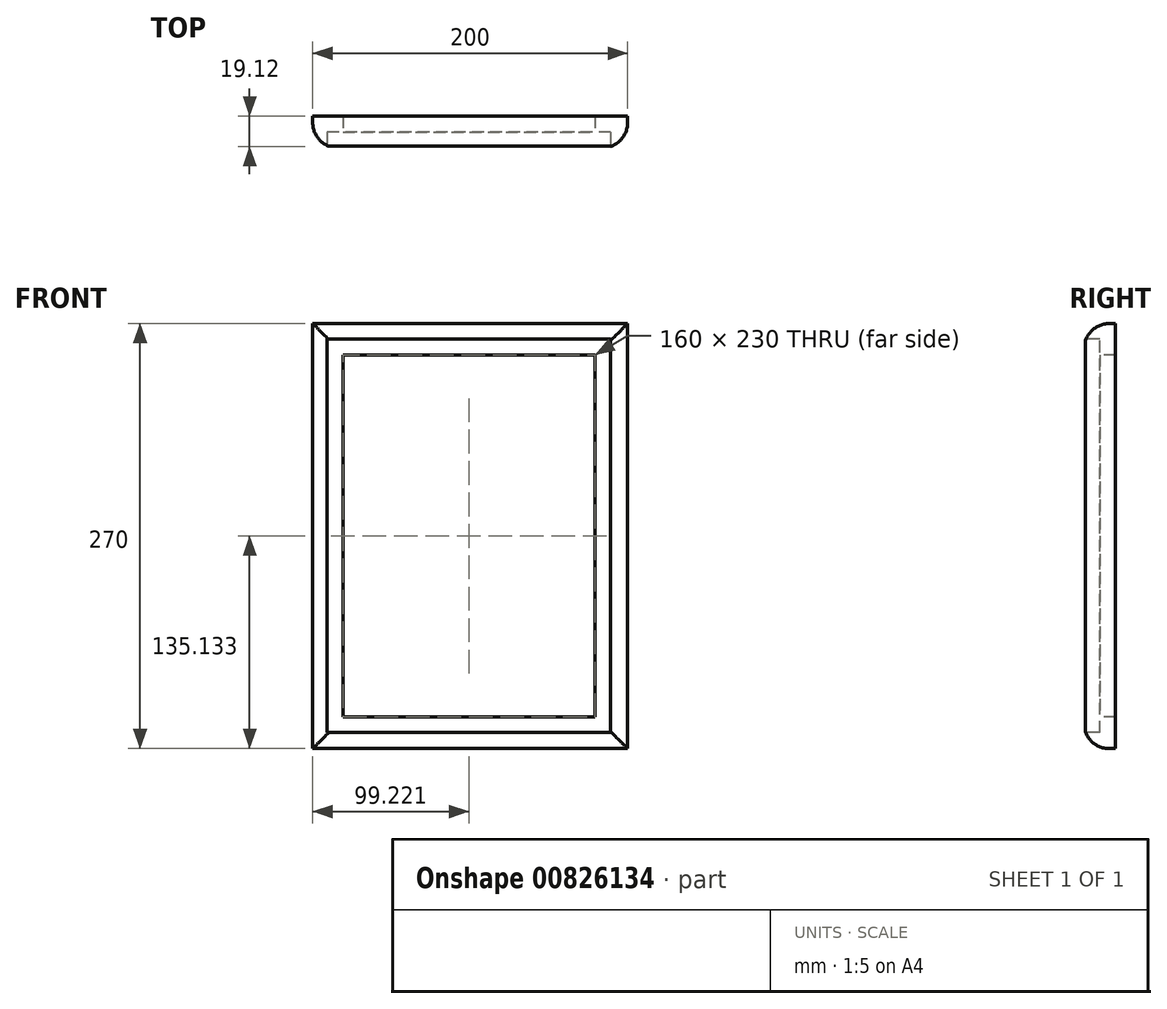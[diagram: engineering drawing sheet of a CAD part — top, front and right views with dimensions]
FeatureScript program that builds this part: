
annotation { "Feature Type Name" : "Feature", "Feature Type Description" : "" }
export const myFeature = defineFeature(function(context is Context, id is Id, definition is map)
    precondition{}
    {
        {
            var Q0;
            Q0=qCreatedBy(makeId("Front.planeOp"),FACE);
            var sketch = newSketch(context, id + "F0", { "sketchPlane" : qUnion([Q0])});
            skLineSegment(sketch, "E0.bottom", {"start": v(78.23, -133.71) * mm, "end": v(-121.77, -133.71) * mm});
            skLineSegment(sketch, "E0.top", {"start": v(78.23, 136.29) * mm, "end": v(-121.77, 136.29) * mm});
            skLineSegment(sketch, "E0.left", {"start": v(78.23, -133.71) * mm, "end": v(78.23, 136.29) * mm});
            skLineSegment(sketch, "E0.right", {"start": v(-121.77, -133.71) * mm, "end": v(-121.77, 136.29) * mm});
            skSolve(sketch);
        }
        {
            var Q0;
            Q0 = qSketchRegion(id + "F0", true);
            extrude(context, id + "F1", {"entities" : qUnion([Q0]), "depth" : 20 * mm, "offsetDistance" : 25 * mm});
        }
        {
            var Q0;
            Q0=makeQuery(id+"F1.opExtrude","CAP_FACE",FACE,{"disambiguationData":[OSD([sQuery(id+"F0.wireOp",EDGE,"E0.bottom"),sQuery(id+"F0.wireOp",EDGE,"E0.top"),sQuery(id+"F0.wireOp",EDGE,"E0.left"),sQuery(id+"F0.wireOp",EDGE,"E0.right")])],"isStart":false});
            var sketch = newSketch(context, id + "F2", { "sketchPlane" : qUnion([Q0])});
            skLineSegment(sketch, "E1.bottom", {"start": v(67.45, -123.58) * mm, "end": v(-112.55, -123.58) * mm});
            skLineSegment(sketch, "E1.top", {"start": v(67.45, 126.42) * mm, "end": v(-112.55, 126.42) * mm});
            skLineSegment(sketch, "E1.left", {"start": v(67.45, -123.58) * mm, "end": v(67.45, 126.42) * mm});
            skLineSegment(sketch, "E1.right", {"start": v(-112.55, -123.58) * mm, "end": v(-112.55, 126.42) * mm});
            skSolve(sketch);
        }
        {
            var Q0;
            Q0 = qSketchRegion(id + "F2", true);
            extrude(context, id + "F3", {"entities" : qUnion([Q0]), "operationType" : NewBodyOperationType.REMOVE, "oppositeDirection" : true, "depth" : 10 * mm, "offsetDistance" : 25 * mm});
        }
        {
            var Q0;
            Q0=makeQuery(id+"F3.boolean.opBoolean","COPY",FACE,{"derivedFrom":makeQuery(id+"F3.opExtrude","CAP_FACE",FACE,{"disambiguationData":[OSD([sQuery(id+"F2.wireOp",EDGE,"E1.bottom"),sQuery(id+"F2.wireOp",EDGE,"E1.top"),sQuery(id+"F2.wireOp",EDGE,"E1.left"),sQuery(id+"F2.wireOp",EDGE,"E1.right")])],"isStart":false})});
            var sketch = newSketch(context, id + "F4", { "sketchPlane" : qUnion([Q0])});
            skLineSegment(sketch, "E2.bottom", {"start": v(-102.55, 116.42) * mm, "end": v(57.45, 116.42) * mm});
            skLineSegment(sketch, "E2.top", {"start": v(-102.55, -113.58) * mm, "end": v(57.45, -113.58) * mm});
            skLineSegment(sketch, "E2.left", {"start": v(-102.55, 116.42) * mm, "end": v(-102.55, -113.58) * mm});
            skLineSegment(sketch, "E2.right", {"start": v(57.45, 116.42) * mm, "end": v(57.45, -113.58) * mm});
            skSolve(sketch);
        }
        {
            var Q0;
            Q0 = qSketchRegion(id + "F4", true);
            extrude(context, id + "F5", {"entities" : qUnion([Q0]), "operationType" : NewBodyOperationType.REMOVE, "oppositeDirection" : true, "depth" : 25 * mm, "offsetDistance" : 25 * mm});
        }
        {
            var Q0;
            Q0=makeQuery(id+"F1.opExtrude","CAP_EDGE",EDGE,{"disambiguationData":[OSD([sQuery(id+"F0.wireOp",EDGE,"E0.right")])],"isStart":false});
            var Q1;
            Q1=makeQuery(id+"F1.opExtrude","CAP_EDGE",EDGE,{"disambiguationData":[OSD([sQuery(id+"F0.wireOp",EDGE,"E0.top")])],"isStart":false});
            var Q2;
            Q2=makeQuery(id+"F1.opExtrude","CAP_EDGE",EDGE,{"disambiguationData":[OSD([sQuery(id+"F0.wireOp",EDGE,"E0.left")])],"isStart":false});
            var Q3;
            Q3=makeQuery(id+"F1.opExtrude","CAP_EDGE",EDGE,{"disambiguationData":[OSD([sQuery(id+"F0.wireOp",EDGE,"E0.bottom")])],"isStart":false});
            fillet(context, id + "F6", {"entities" : qUnion([Q0, Q1, Q2, Q3]), "radius" : 16 * mm, "tangentPropagation" : true, "allowEdgeOverflow" : false});
        }
    });
